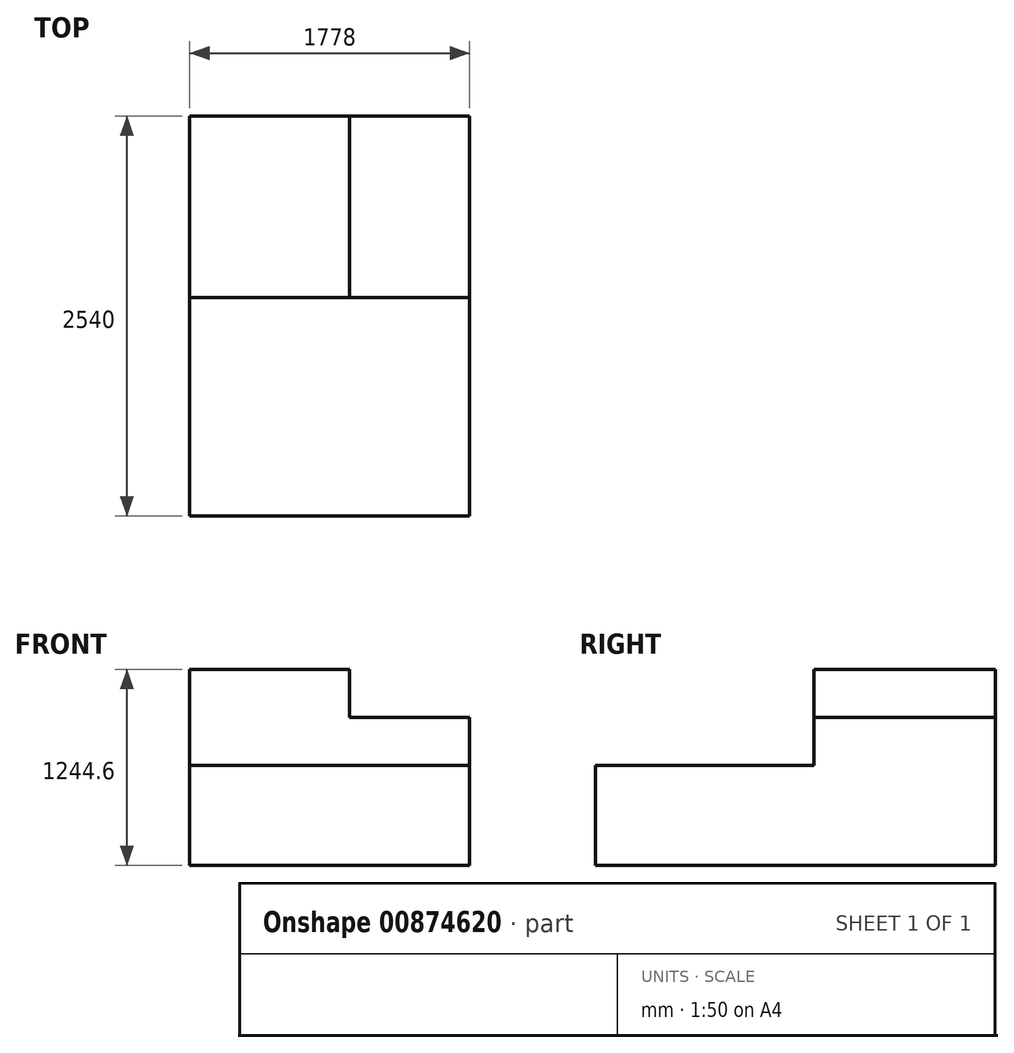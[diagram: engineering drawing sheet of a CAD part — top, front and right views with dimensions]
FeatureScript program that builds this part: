
annotation { "Feature Type Name" : "Feature", "Feature Type Description" : "" }
export const myFeature = defineFeature(function(context is Context, id is Id, definition is map)
    precondition{}
    {
        {
            var Q0;
            Q0=qCreatedBy(makeId("Top.planeOp"),FACE);
            var sketch = newSketch(context, id + "F0", { "sketchPlane" : qUnion([Q0])});
            skLineSegment(sketch, "E0.bottom", {"start": v(0, 0) * mm, "end": v(-1778, 0) * mm});
            skLineSegment(sketch, "E0.top", {"start": v(0, -2540) * mm, "end": v(-1778, -2540) * mm});
            skLineSegment(sketch, "E0.left", {"start": v(0, 0) * mm, "end": v(0, -2540) * mm});
            skLineSegment(sketch, "E0.right", {"start": v(-1778, 0) * mm, "end": v(-1778, -2540) * mm});
            skSolve(sketch);
        }
        {
            var Q0;
            Q0=makeQuery(id+"F0.imprint","IMPRINT",FACE,{"disambiguationData":[TD([[makeQuery(id+"F0.imprint","IMPRINT",EDGE,{"derivedFrom":sQuery(id+"F0.wireOp",EDGE,"E0.bottom")}),1.0]])]});
            extrude(context, id + "F1", {"entities" : qUnion([Q0]), "depth" : 635 * mm, "offsetDistance" : 25.4 * mm});
        }
        {
            var Q0;
            Q0=makeQuery(id+"F1.opExtrude","CAP_FACE",FACE,{"disambiguationData":[OSD([sQuery(id+"F0.wireOp",EDGE,"E0.bottom"),sQuery(id+"F0.wireOp",EDGE,"E0.top"),sQuery(id+"F0.wireOp",EDGE,"E0.left"),sQuery(id+"F0.wireOp",EDGE,"E0.right")])],"isStart":false});
            var sketch = newSketch(context, id + "F2", { "sketchPlane" : qUnion([Q0])});
            skLineSegment(sketch, "E1.bottom", {"start": v(-1778, 0) * mm, "end": v(0, 0) * mm});
            skLineSegment(sketch, "E1.top", {"start": v(-1778, -1153.8) * mm, "end": v(0, -1153.8) * mm});
            skLineSegment(sketch, "E1.left", {"start": v(-1778, 0) * mm, "end": v(-1778, -1153.8) * mm});
            skLineSegment(sketch, "E1.right", {"start": v(0, 0) * mm, "end": v(0, -1153.8) * mm});
            skLineSegment(sketch, "E2.bottom", {"start": v(2261.1, -3884.31) * mm, "end": v(1539.17, -3884.31) * mm});
            skLineSegment(sketch, "E2.top", {"start": v(2261.1, -2779.19) * mm, "end": v(1539.17, -2779.19) * mm});
            skLineSegment(sketch, "E2.left", {"start": v(2261.1, -3884.31) * mm, "end": v(2261.1, -2779.19) * mm});
            skLineSegment(sketch, "E2.right", {"start": v(1539.17, -3884.31) * mm, "end": v(1539.17, -2779.19) * mm});
            skSolve(sketch);
        }
        {
            var Q0;
            Q0=makeQuery(id+"F2.imprint","IMPRINT",FACE,{"disambiguationData":[TD([[makeQuery(id+"F2.imprint","IMPRINT",EDGE,{"derivedFrom":sQuery(id+"F2.wireOp",EDGE,"E1.bottom")}),1.0]])]});
            extrude(context, id + "F3", {"entities" : qUnion([Q0]), "operationType" : NewBodyOperationType.ADD, "depth" : 304.8 * mm, "offsetDistance" : 25.4 * mm});
        }
        {
            var Q0;
            Q0=makeQuery(id+"F3.opExtrude","CAP_FACE",FACE,{"disambiguationData":[OSD([sQuery(id+"F2.wireOp",EDGE,"E1.bottom"),sQuery(id+"F2.wireOp",EDGE,"E1.top"),sQuery(id+"F2.wireOp",EDGE,"E1.left"),sQuery(id+"F2.wireOp",EDGE,"E1.right")])],"isStart":false});
            var sketch = newSketch(context, id + "F4", { "sketchPlane" : qUnion([Q0])});
            skLineSegment(sketch, "E3.bottom", {"start": v(-1778, 0) * mm, "end": v(-762, 0) * mm});
            skLineSegment(sketch, "E3.top", {"start": v(-1778, -1153.8) * mm, "end": v(-762, -1153.8) * mm});
            skLineSegment(sketch, "E3.left", {"start": v(-1778, 0) * mm, "end": v(-1778, -1153.8) * mm});
            skLineSegment(sketch, "E3.right", {"start": v(-762, 0) * mm, "end": v(-762, -1153.8) * mm});
            skSolve(sketch);
        }
        {
            var Q0;
            Q0=makeQuery(id+"F4.imprint","IMPRINT",FACE,{"disambiguationData":[TD([[makeQuery(id+"F4.imprint","IMPRINT",EDGE,{"derivedFrom":sQuery(id+"F4.wireOp",EDGE,"E3.bottom")}),1.0]])]});
            extrude(context, id + "F5", {"entities" : qUnion([Q0]), "operationType" : NewBodyOperationType.ADD, "depth" : 304.8 * mm, "offsetDistance" : 25.4 * mm});
        }
    });
